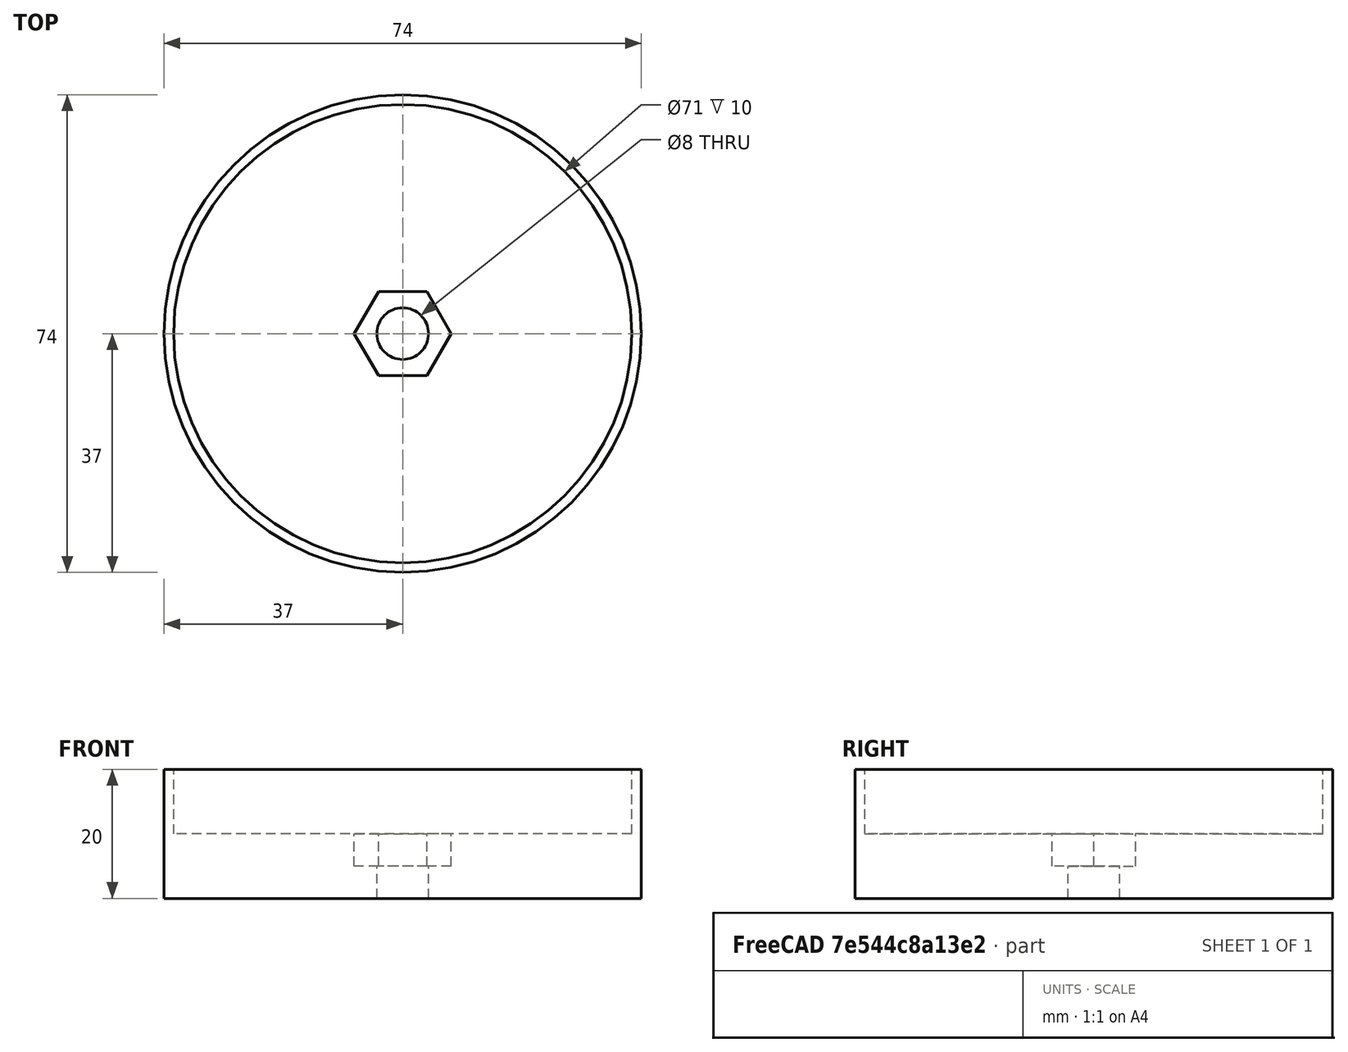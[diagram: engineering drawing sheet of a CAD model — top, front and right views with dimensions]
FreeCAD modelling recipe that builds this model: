
FCSTD DOCUMENT  (FreeCAD 0.18.4R)
Label: cup_holder
License: All rights reserved
LicenseURL: http://en.wikipedia.org/wiki/All_rights_reserved
objects: Part::Cylinder×3, Part::Cut×3, Part::Part2DObjectPython×1, Part::Extrusion×1, Part::MultiCommon×1
note: 9 computed .brp shape members not serialized (recipe doc carries the construction recipe); baked Part::Feature solids carry a one-line shape summary decoded from their .brp

FEATURE [Part::Cylinder] Cylinder
  Angle = 360
  AttacherType = Attacher::AttachEngine3D
  Height = 20
  Radius = 37
FEATURE [Part::Part2DObjectPython] Polygon  # Draft 2D object (typed FeaturePython)
  ChamferSize = 0
  DrawMode = 0
  FacesNumber = 6
  FilletRadius = 0
  MakeFace = true
  Radius = 7.505
FEATURE [Part::Extrusion] Extrude
  Base = -> Polygon
  Dir = (0,0,1)
  DirMode = 2
  FaceMakerClass = Part::FaceMakerBullseye
  LengthFwd = 5
  LengthRev = 0
  Placement = pos=(0,0,5) rot=(0,0,1;0rad)
  Solid = false
  Symmetric = false
FEATURE [Part::Cylinder] Cylinder001
  Angle = 360
  AttacherType = Attacher::AttachEngine3D
  Height = 10
  Placement = pos=(0,0,10) rot=(0,0,1;0rad)
  Radius = 35.5
FEATURE [Part::Cylinder] Cylinder002
  Angle = 360
  AttacherType = Attacher::AttachEngine3D
  Height = 5
  Radius = 4
FEATURE [Part::Cut] Cut
  Base = -> Cylinder
  Tool = -> Extrude
FEATURE [Part::Cut] Cut001
  Base = -> Cylinder
  Tool = -> Cylinder001
FEATURE [Part::Cut] Cut002
  Base = -> Cylinder
  Tool = -> Cylinder002
FEATURE [Part::MultiCommon] Common
  Shapes = -> [Cut002,Cut,Cut001]
